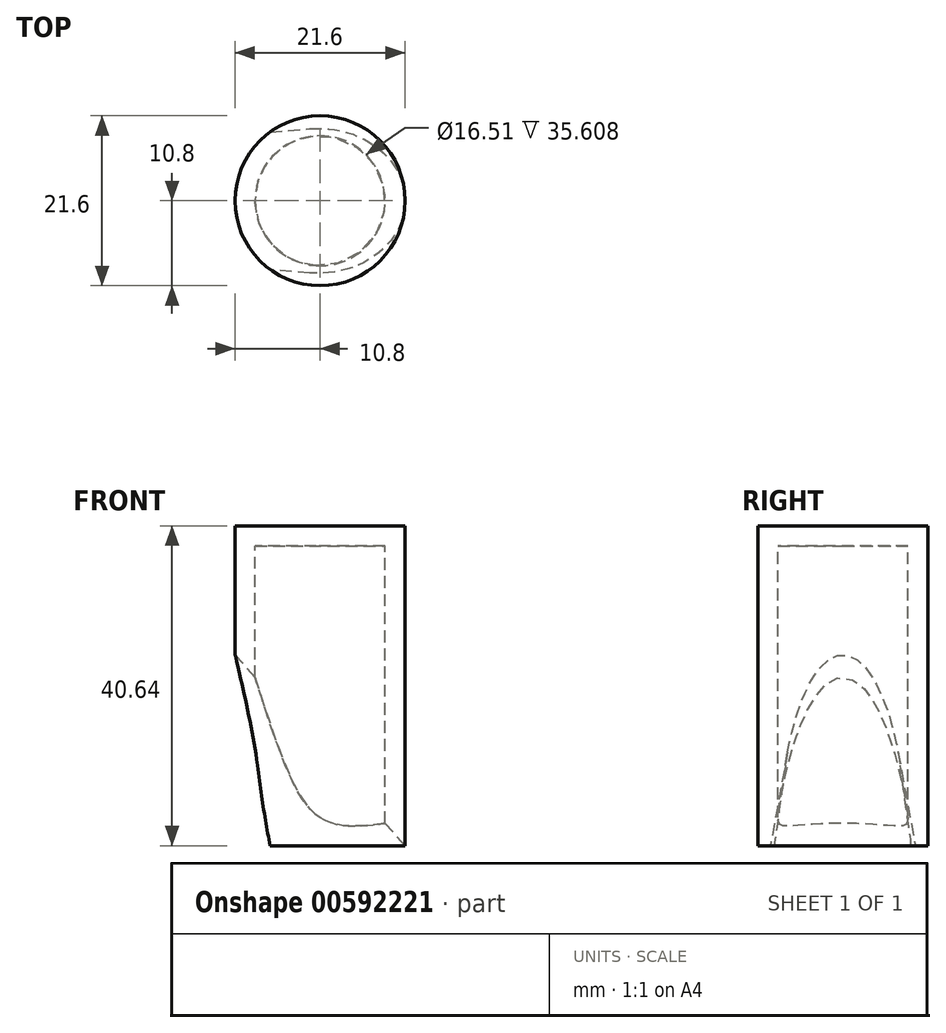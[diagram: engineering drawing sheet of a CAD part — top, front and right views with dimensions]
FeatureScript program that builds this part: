
annotation { "Feature Type Name" : "Feature", "Feature Type Description" : "" }
export const myFeature = defineFeature(function(context is Context, id is Id, definition is map)
    precondition{}
    {
        {
            var Q0;
            Q0=qCreatedBy(makeId("Top.planeOp"),FACE);
            var sketch = newSketch(context, id + "F0", { "sketchPlane" : qUnion([Q0])});
            skCircle(sketch, "E0", {"center": v(0, 0) * mm, "radius": 10.8 * mm});
            skSolve(sketch);
        }
        {
            var Q0;
            Q0 = qSketchRegion(id + "F0", true);
            extrude(context, id + "F1", {"entities" : qUnion([Q0]), "depth" : 2.54 * mm, "offsetDistance" : 25.4 * mm});
        }
        {
            var Q0;
            Q0=makeQuery(id+"F1.opExtrude","CAP_FACE",FACE,{"disambiguationData":[OSD([sQuery(id+"F0.wireOp",EDGE,"E0")])],"isStart":true});
            var sketch = newSketch(context, id + "F2", { "sketchPlane" : qUnion([Q0])});
            skCircle(sketch, "E1.0", {"center": v(0, 0) * mm, "radius": 8.26 * mm});
            skSolve(sketch);
        }
        {
            var Q0;
            Q0=makeQuery(id+"F2.imprint","IMPRINT",FACE,{"disambiguationData":[TD([[makeQuery(id+"F2.imprint","IMPRINT",EDGE,{"derivedFrom":sQuery(id+"F2.wireOp",EDGE,"E1.0")}),-1.0]])]});
            extrude(context, id + "F3", {"entities" : qUnion([Q0]), "operationType" : NewBodyOperationType.ADD, "depth" : 38.1 * mm, "offsetDistance" : 25.4 * mm});
        }
        {
            var Q0;
            Q0=makeQuery(id+"F3.opExtrude","CAP_FACE",FACE,{"disambiguationData":[OSD([sQuery(id+"F0.wireOp",EDGE,"E0"),sQuery(id+"F2.wireOp",EDGE,"E1.0")])],"isStart":false});
            var sketch = newSketch(context, id + "F4", { "sketchPlane" : qUnion([Q0])});
            skLineSegment(sketch, "E2", {"start": v(10.8, 0) * mm, "end": v(10.8, 10.8) * mm});
            skLineSegment(sketch, "E3", {"start": v(10.8, 0) * mm, "end": v(10.8, -10.8) * mm});
            skSolve(sketch);
        }
        {
            var Q0;
            Q0=sQuery(id+"F4.wireOp",EDGE,"E3");
            cPlane(context, id + "F5", {"entities" : qUnion([Q0]), "cplaneType" : CPlaneType.LINE_ANGLE, "offset" : 25.4 * mm, "angle" : 33 * degree, "oppositeDirection" : true, "width" : 152.4 * mm, "height" : 152.4 * mm});
        }
        {
            var Q0;
            Q0=qCreatedBy(id+"F5.planeOp",FACE);
            var sketch = newSketch(context, id + "F6", { "sketchPlane" : qUnion([Q0])});
            skArc(sketch, "E4", {"start": v(-21.86, -10.16) * mm, "mid": v(-11.7, 0) * mm, "end": v(-21.86, 10.16) * mm});
            skLineSegment(sketch, "E5", {"start": v(-21.86, -10.16) * mm, "end": v(-34.56, -10.16) * mm});
            skLineSegment(sketch, "E6", {"start": v(-21.86, 10.16) * mm, "end": v(-34.56, 10.16) * mm});
            skLineSegment(sketch, "E7", {"start": v(-34.56, -10.16) * mm, "end": v(-34.56, 10.16) * mm});
            skSolve(sketch);
        }
        {
            var Q0;
            Q0 = qSketchRegion(id + "F6", true);
            extrude(context, id + "F7", {"entities" : qUnion([Q0]), "operationType" : NewBodyOperationType.REMOVE, "endBound" : BoundingType.THROUGH_ALL, "depth" : 25.4 * mm, "offsetDistance" : 25.4 * mm, "hasDraft" : true, "draftAngle" : 8.68 * degree, "draftPullDirection" : true});
        }
    });
